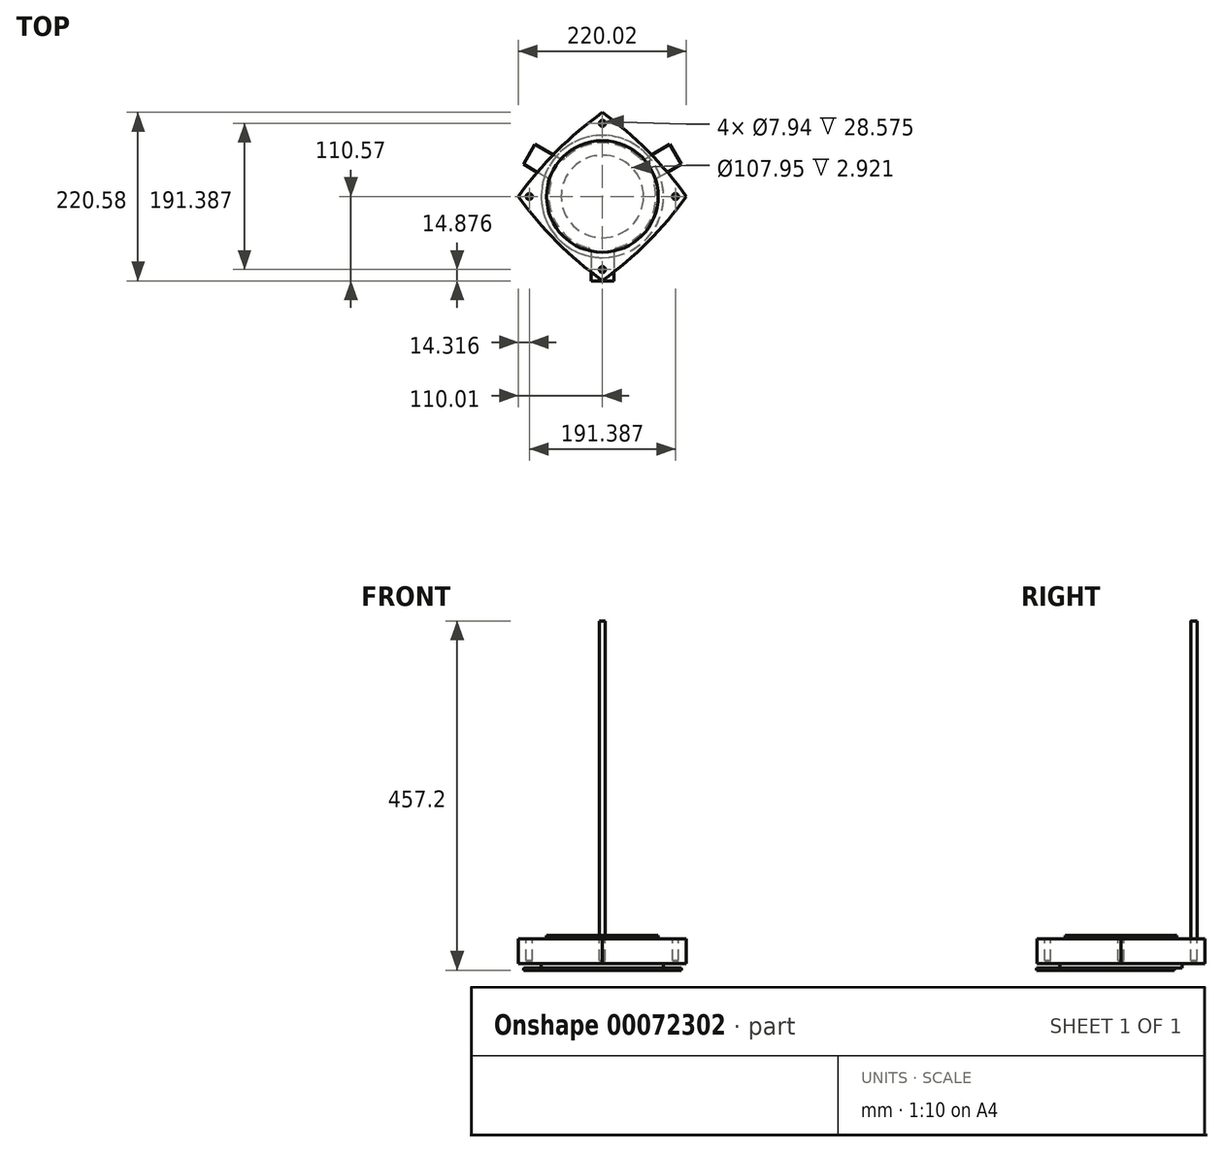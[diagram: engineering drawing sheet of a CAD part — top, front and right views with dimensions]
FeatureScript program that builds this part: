
annotation { "Feature Type Name" : "Feature", "Feature Type Description" : "" }
export const myFeature = defineFeature(function(context is Context, id is Id, definition is map)
    precondition{}
    {
        {
            var Q0;
            Q0=qCreatedBy(makeId("Top.planeOp"),FACE);
            var sketch = newSketch(context, id + "F0", { "sketchPlane" : qUnion([Q0])});
            skCircle(sketch, "E0", {"center": v(0, 0) * mm, "radius": 73.03 * mm});
            skSolve(sketch);
        }
        {
            var Q0;
            Q0 = qSketchRegion(id + "F0", true);
            extrude(context, id + "F1", {"entities" : qUnion([Q0]), "oppositeDirection" : true, "depth" : 4.76 * mm});
        }
        {
            var Q0;
            Q0=makeQuery(id+"F1.opExtrude","CAP_FACE",FACE,{"disambiguationData":[OSD([sQuery(id+"F0.wireOp",EDGE,"E0")])],"isStart":false});
            var sketch = newSketch(context, id + "F2", { "sketchPlane" : qUnion([Q0])});
            skLineSegment(sketch, "E1.rect.bottom", {"start": v(77.79, 77.79) * mm, "end": v(-77.79, 77.79) * mm, "construction": true});
            skLineSegment(sketch, "E1.rect.top", {"start": v(77.79, -77.79) * mm, "end": v(-77.79, -77.79) * mm, "construction": true});
            skLineSegment(sketch, "E1.rect.left", {"start": v(77.79, 77.79) * mm, "end": v(77.79, -77.79) * mm, "construction": true});
            skLineSegment(sketch, "E1.rect.right", {"start": v(-77.79, 77.79) * mm, "end": v(-77.79, -77.79) * mm, "construction": true});
            skPoint(sketch, "E1.rect.middle", {"position": v(0, 0) * mm});
            skArc(sketch, "E2", {"start": v(-77.79, -77.79) * mm, "mid": v(0, -84.14) * mm, "end": v(77.79, -77.79) * mm});
            skArc(sketch, "E3", {"start": v(77.79, -77.79) * mm, "mid": v(84.14, 0) * mm, "end": v(77.79, 77.79) * mm});
            skArc(sketch, "E4", {"start": v(77.79, 77.79) * mm, "mid": v(0, 84.14) * mm, "end": v(-77.79, 77.79) * mm});
            skArc(sketch, "E5", {"start": v(-77.79, 77.79) * mm, "mid": v(-84.14, 0) * mm, "end": v(-77.79, -77.79) * mm});
            skSolve(sketch);
        }
        {
            var Q0;
            Q0 = qSketchRegion(id + "F2", true);
            extrude(context, id + "F3", {"entities" : qUnion([Q0]), "operationType" : NewBodyOperationType.ADD, "depth" : 32 * mm});
        }
        {
            var Q0;
            Q0=makeQuery(id+"F3.opExtrude","CAP_FACE",FACE,{"disambiguationData":[OSD([sQuery(id+"F2.wireOp",EDGE,"E2"),sQuery(id+"F2.wireOp",EDGE,"E3"),sQuery(id+"F2.wireOp",EDGE,"E4"),sQuery(id+"F2.wireOp",EDGE,"E5")])],"isStart":true});
            var sketch = newSketch(context, id + "F4", { "sketchPlane" : qUnion([Q0])});
            skCircle(sketch, "E6", {"center": v(-67.67, 67.67) * mm, "radius": 3.97 * mm});
            skCircle(sketch, "E7.1.0", {"center": v(-67.67, -67.67) * mm, "radius": 3.97 * mm});
            skCircle(sketch, "E7.2.0", {"center": v(67.67, -67.67) * mm, "radius": 3.97 * mm});
            skCircle(sketch, "E7.3.0", {"center": v(67.67, 67.67) * mm, "radius": 3.97 * mm});
            skPoint(sketch, "E7.center", {"position": v(0, 0) * mm});
            skSolve(sketch);
        }
        {
            var Q0;
            Q0 = qSketchRegion(id + "F4", true);
            extrude(context, id + "F5", {"entities" : qUnion([Q0]), "operationType" : NewBodyOperationType.REMOVE, "oppositeDirection" : true, "depth" : 28.57 * mm});
        }
        {
            var Q0;
            Q0=makeQuery(id+"F3.opExtrude","CAP_FACE",FACE,{"disambiguationData":[OSD([sQuery(id+"F2.wireOp",EDGE,"E2"),sQuery(id+"F2.wireOp",EDGE,"E3"),sQuery(id+"F2.wireOp",EDGE,"E4"),sQuery(id+"F2.wireOp",EDGE,"E5")])],"isStart":false});
            var sketch = newSketch(context, id + "F6", { "sketchPlane" : qUnion([Q0])});
            skCircle(sketch, "E8", {"center": v(0, 0) * mm, "radius": 80.01 * mm});
            skSolve(sketch);
        }
        {
            var Q0;
            Q0 = qSketchRegion(id + "F6", true);
            extrude(context, id + "F7", {"entities" : qUnion([Q0]), "operationType" : NewBodyOperationType.ADD, "depth" : 6.03 * mm});
        }
        {
            var Q0;
            Q0=qCreatedBy(makeId("Front.planeOp"),FACE);
            var sketch = newSketch(context, id + "F8", { "sketchPlane" : qUnion([Q0])});
            skLineSegment(sketch, "E9", {"start": v(0, 0) * mm, "end": v(0, 64.25) * mm});
            skSolve(sketch);
        }
        {
            var Q0;
            Q0=makeQuery(id+"F1.opExtrude","SWEPT_BODY",BODY,{"disambiguationData":[OSD([sQuery(id+"F0.wireOp",EDGE,"E0")])]});
            var Q1;
            Q1=sQuery(id+"F8.wireOp",EDGE,"E9");
            transform(context, id + "F9", {"entities" : qUnion([Q0]), "transformType" : TransformType.ROTATION, "transformAxis" : qUnion([Q1]), "angle" : 45 * degree, "oppositeDirection" : true, "makeCopy" : false});
        }
        {
            var Q0;
            Q0=makeQuery(id+"F7.opExtrude","CAP_FACE",FACE,{"disambiguationData":[OSD([sQuery(id+"F6.wireOp",EDGE,"E8")])],"isStart":false});
            var sketch = newSketch(context, id + "F10", { "sketchPlane" : qUnion([Q0])});
            skCircle(sketch, "E10", {"center": v(0, 0) * mm, "radius": 69.98 * mm});
            skLineSegment(sketch, "E11.bottom", {"start": v(-14.99, 68.35) * mm, "end": v(14.99, 68.35) * mm});
            skLineSegment(sketch, "E11.top", {"start": v(-14.99, 110.57) * mm, "end": v(14.99, 110.57) * mm});
            skLineSegment(sketch, "E11.left", {"start": v(-14.99, 68.35) * mm, "end": v(-14.99, 110.57) * mm});
            skLineSegment(sketch, "E11.right", {"start": v(14.99, 68.35) * mm, "end": v(14.99, 110.57) * mm});
            skCircle(sketch, "E12", {"center": v(0, 0) * mm, "radius": 53.98 * mm});
            skLineSegment(sketch, "E13", {"start": v(0, 0) * mm, "end": v(0, 68.35) * mm, "construction": true});
            skLineSegment(sketch, "E14.1.0", {"start": v(-51.7, -47.16) * mm, "end": v(-88.26, -68.26) * mm});
            skLineSegment(sketch, "E14.1.1", {"start": v(-51.7, -47.16) * mm, "end": v(-66.69, -21.2) * mm});
            skLineSegment(sketch, "E14.1.2", {"start": v(-66.69, -21.2) * mm, "end": v(-103.25, -42.3) * mm});
            skLineSegment(sketch, "E14.1.3", {"start": v(-88.26, -68.26) * mm, "end": v(-103.25, -42.3) * mm});
            skLineSegment(sketch, "E14.2.0", {"start": v(66.69, -21.2) * mm, "end": v(103.25, -42.3) * mm});
            skLineSegment(sketch, "E14.2.1", {"start": v(66.69, -21.2) * mm, "end": v(51.7, -47.16) * mm});
            skLineSegment(sketch, "E14.2.2", {"start": v(51.7, -47.16) * mm, "end": v(88.26, -68.26) * mm});
            skLineSegment(sketch, "E14.2.3", {"start": v(103.25, -42.3) * mm, "end": v(88.26, -68.26) * mm});
            skSolve(sketch);
        }
        {
            var Q0;
            {var subQ0=sQuery(id+"F10.wireOp",EDGE,"E11.bottom");Q0=makeQuery(id+"F10.imprint","IMPRINT",FACE,{"disambiguationData":[TD([[makeQuery(id+"F10.imprint","IMPRINT",EDGE,{"derivedFrom":subQ0}),1.0]])]});}
            var Q1;
            {var subQ0=sQuery(id+"F10.wireOp",EDGE,"E14.1.1");Q1=makeQuery(id+"F10.imprint","IMPRINT",FACE,{"disambiguationData":[TD([[makeQuery(id+"F10.imprint","IMPRINT",EDGE,{"derivedFrom":subQ0}),1.0]])]});}
            var Q2;
            {var subQ0=sQuery(id+"F10.wireOp",EDGE,"E14.2.1");Q2=makeQuery(id+"F10.imprint","IMPRINT",FACE,{"disambiguationData":[TD([[makeQuery(id+"F10.imprint","IMPRINT",EDGE,{"derivedFrom":subQ0}),1.0]])]});}
            var Q3;
            {var subQ0=sQuery(id+"F10.wireOp",EDGE,"E11.bottom");Q3=makeQuery(id+"F10.imprint","IMPRINT",FACE,{"disambiguationData":[TD([[makeQuery(id+"F10.imprint","IMPRINT",EDGE,{"derivedFrom":subQ0}),-1.0]])]});}
            var Q4;
            {var subQ0=sQuery(id+"F10.wireOp",EDGE,"E14.1.3");Q4=makeQuery(id+"F10.imprint","IMPRINT",FACE,{"disambiguationData":[TD([[makeQuery(id+"F10.imprint","IMPRINT",EDGE,{"derivedFrom":subQ0}),-1.0]])]});}
            var Q5;
            {var subQ0=sQuery(id+"F10.wireOp",EDGE,"E14.2.3");Q5=makeQuery(id+"F10.imprint","IMPRINT",FACE,{"disambiguationData":[TD([[makeQuery(id+"F10.imprint","IMPRINT",EDGE,{"derivedFrom":subQ0}),-1.0]])]});}
            var Q6;
            {var subQ0=sQuery(id+"F10.wireOp",EDGE,"E11.left");var subQ6=makeQuery(id+"F7.opExtrude","CAP_EDGE",EDGE,{"disambiguationData":[OSD([sQuery(id+"F6.wireOp",EDGE,"E8")])],"isStart":false});var subQ7=makeQuery(id+"F10.imprint","INTERSECT",VERTEX,{"derivedFrom":[subQ6,subQ0]});Q6=makeQuery(id+"F10.imprint","IMPRINT",FACE,{"disambiguationData":[TD([[makeQuery(id+"F10.imprint","IMPRINT",EDGE,{"disambiguationData":[TD([[subQ7,1.0]])],"derivedFrom":subQ6}),1.0]])]});}
            var Q7;
            {var subQ1=sQuery(id+"F10.wireOp",EDGE,"E14.1.0");var subQ6=makeQuery(id+"F7.opExtrude","CAP_EDGE",EDGE,{"disambiguationData":[OSD([sQuery(id+"F6.wireOp",EDGE,"E8")])],"isStart":false});var subQ7=makeQuery(id+"F10.imprint","INTERSECT",VERTEX,{"derivedFrom":[subQ6,subQ1]});Q7=makeQuery(id+"F10.imprint","IMPRINT",FACE,{"disambiguationData":[TD([[makeQuery(id+"F10.imprint","IMPRINT",EDGE,{"disambiguationData":[TD([[subQ7,1.0]])],"derivedFrom":subQ6}),1.0]])]});}
            var Q8;
            {var subQ1=sQuery(id+"F10.wireOp",EDGE,"E14.2.0");var subQ6=makeQuery(id+"F7.opExtrude","CAP_EDGE",EDGE,{"disambiguationData":[OSD([sQuery(id+"F6.wireOp",EDGE,"E8")])],"isStart":false});var subQ7=makeQuery(id+"F10.imprint","INTERSECT",VERTEX,{"derivedFrom":[subQ6,subQ1]});Q8=makeQuery(id+"F10.imprint","IMPRINT",FACE,{"disambiguationData":[TD([[makeQuery(id+"F10.imprint","IMPRINT",EDGE,{"disambiguationData":[TD([[subQ7,1.0]])],"derivedFrom":subQ6}),1.0]])]});}
            var Q9;
            {var subQ0=sQuery(id+"F10.wireOp",EDGE,"E11.top");Q9=makeQuery(id+"F10.imprint","IMPRINT",FACE,{"disambiguationData":[TD([[makeQuery(id+"F10.imprint","IMPRINT",EDGE,{"derivedFrom":subQ0}),-1.0]])]});}
            extrude(context, id + "F11", {"entities" : qUnion([Q0, Q1, Q2, Q3, Q4, Q5, Q6, Q7, Q8, Q9]), "operationType" : NewBodyOperationType.ADD, "depth" : 2.92 * mm});
        }
        {
            var Q0;
            Q0=makeQuery(id+"F3.opExtrude","CAP_FACE",FACE,{"disambiguationData":[OSD([sQuery(id+"F2.wireOp",EDGE,"E2"),sQuery(id+"F2.wireOp",EDGE,"E3"),sQuery(id+"F2.wireOp",EDGE,"E4"),sQuery(id+"F2.wireOp",EDGE,"E5")])],"isStart":true});
            var sketch = newSketch(context, id + "F12", { "sketchPlane" : qUnion([Q0])});
            skCircle(sketch, "E15", {"center": v(0, 95.7) * mm, "radius": 3.94 * mm});
            skSolve(sketch);
        }
        {
            var Q0;
            Q0 = qSketchRegion(id + "F12", true);
            extrude(context, id + "F13", {"entities" : qUnion([Q0]), "depth" : 416.24 * mm});
        }
        {
            var Q0;
            Q0=makeQuery(id+"F11.opExtrude","SWEPT_EDGE",EDGE,{"disambiguationData":[OSD([sQuery(id+"F10.wireOp",EDGE,"E10"),sQuery(id+"F10.wireOp",EDGE,"E11.bottom"),sQuery(id+"F10.wireOp",EDGE,"E11.right")])]});
            var Q1;
            Q1=makeQuery(id+"F11.opExtrude","SWEPT_EDGE",EDGE,{"disambiguationData":[OSD([sQuery(id+"F10.wireOp",EDGE,"E10"),sQuery(id+"F10.wireOp",EDGE,"E11.bottom"),sQuery(id+"F10.wireOp",EDGE,"E11.left")])]});
            var Q2;
            Q2=makeQuery(id+"F11.opExtrude","SWEPT_EDGE",EDGE,{"disambiguationData":[OSD([sQuery(id+"F10.wireOp",EDGE,"E10"),sQuery(id+"F10.wireOp",EDGE,"E14.1.1"),sQuery(id+"F10.wireOp",EDGE,"E14.1.2")])]});
            var Q3;
            Q3=makeQuery(id+"F11.opExtrude","SWEPT_EDGE",EDGE,{"disambiguationData":[OSD([sQuery(id+"F10.wireOp",EDGE,"E10"),sQuery(id+"F10.wireOp",EDGE,"E14.1.0"),sQuery(id+"F10.wireOp",EDGE,"E14.1.1")])]});
            var Q4;
            Q4=makeQuery(id+"F11.opExtrude","SWEPT_EDGE",EDGE,{"disambiguationData":[OSD([sQuery(id+"F10.wireOp",EDGE,"E10"),sQuery(id+"F10.wireOp",EDGE,"E14.2.1"),sQuery(id+"F10.wireOp",EDGE,"E14.2.2")])]});
            var Q5;
            Q5=makeQuery(id+"F11.opExtrude","SWEPT_EDGE",EDGE,{"disambiguationData":[OSD([sQuery(id+"F10.wireOp",EDGE,"E10"),sQuery(id+"F10.wireOp",EDGE,"E14.2.0"),sQuery(id+"F10.wireOp",EDGE,"E14.2.1")])]});
            fillet(context, id + "F14", {"entities" : qUnion([Q0, Q1, Q2, Q3, Q4, Q5]), "radius" : 4.76 * mm, "tangentPropagation" : true, "allowEdgeOverflow" : false});
        }
    });
